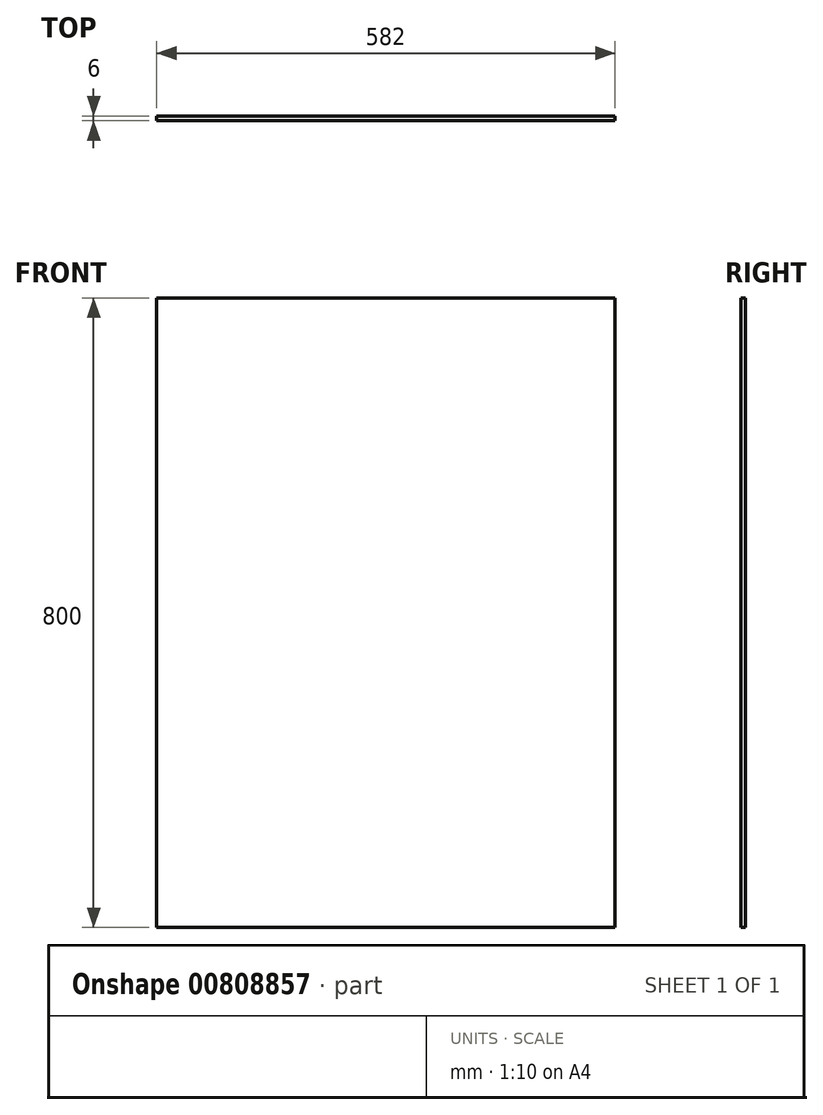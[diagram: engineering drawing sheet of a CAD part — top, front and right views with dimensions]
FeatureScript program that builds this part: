
annotation { "Feature Type Name" : "Feature", "Feature Type Description" : "" }
export const myFeature = defineFeature(function(context is Context, id is Id, definition is map)
    precondition{}
    {
        {
            var Q0;
            Q0=qCreatedBy(makeId("Front.planeOp"),FACE);
            var sketch = newSketch(context, id + "F0", { "sketchPlane" : qUnion([Q0])});
            skLineSegment(sketch, "E0.bottom", {"start": v(0, 0) * mm, "end": v(-582, 0) * mm});
            skLineSegment(sketch, "E0.top", {"start": v(0, 800) * mm, "end": v(-582, 800) * mm});
            skLineSegment(sketch, "E0.left", {"start": v(0, 0) * mm, "end": v(0, 800) * mm});
            skLineSegment(sketch, "E0.right", {"start": v(-582, 0) * mm, "end": v(-582, 800) * mm});
            skSolve(sketch);
        }
        {
            var Q0;
            Q0=makeQuery(id+"F0.imprint","IMPRINT",FACE,{"disambiguationData":[TD([[makeQuery(id+"F0.imprint","IMPRINT",EDGE,{"derivedFrom":sQuery(id+"F0.wireOp",EDGE,"E0.bottom")}),-1.0]])]});
            extrude(context, id + "F1", {"entities" : qUnion([Q0]), "depth" : 6 * mm, "offsetDistance" : 25 * mm});
        }
    });
